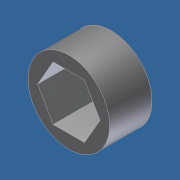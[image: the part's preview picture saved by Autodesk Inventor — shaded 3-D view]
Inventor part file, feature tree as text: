
AUTODESK INVENTOR PART (.ipt)
format: ipt  version: unknown  size: 183,296 bytes
history: native  units: in
note: dims shown in document units (in); Inventor stores cm internally (conversion verified against a paired STEP export)
features: other x1, imported_body x1, extrude x1, sketch x1
ambient origin geometry x8: Origin, YZ Plane, XZ Plane, XY Plane, X Axis, Y Axis, Z Axis, Center Point
feature tree (4):
  other  "Boss-Extrude1"
  imported_body  "Base1"
  extrude  "Extrusion1"  [1 undecoded]
  sketch  "Sketch1"  dims[d0=0.3362in d1=0.0in]
note: 1 required parameter value undecoded (feature->parameter linkage not recoverable at this tier; creation-order binding heuristic only, values carry confidence <= 0.55)
